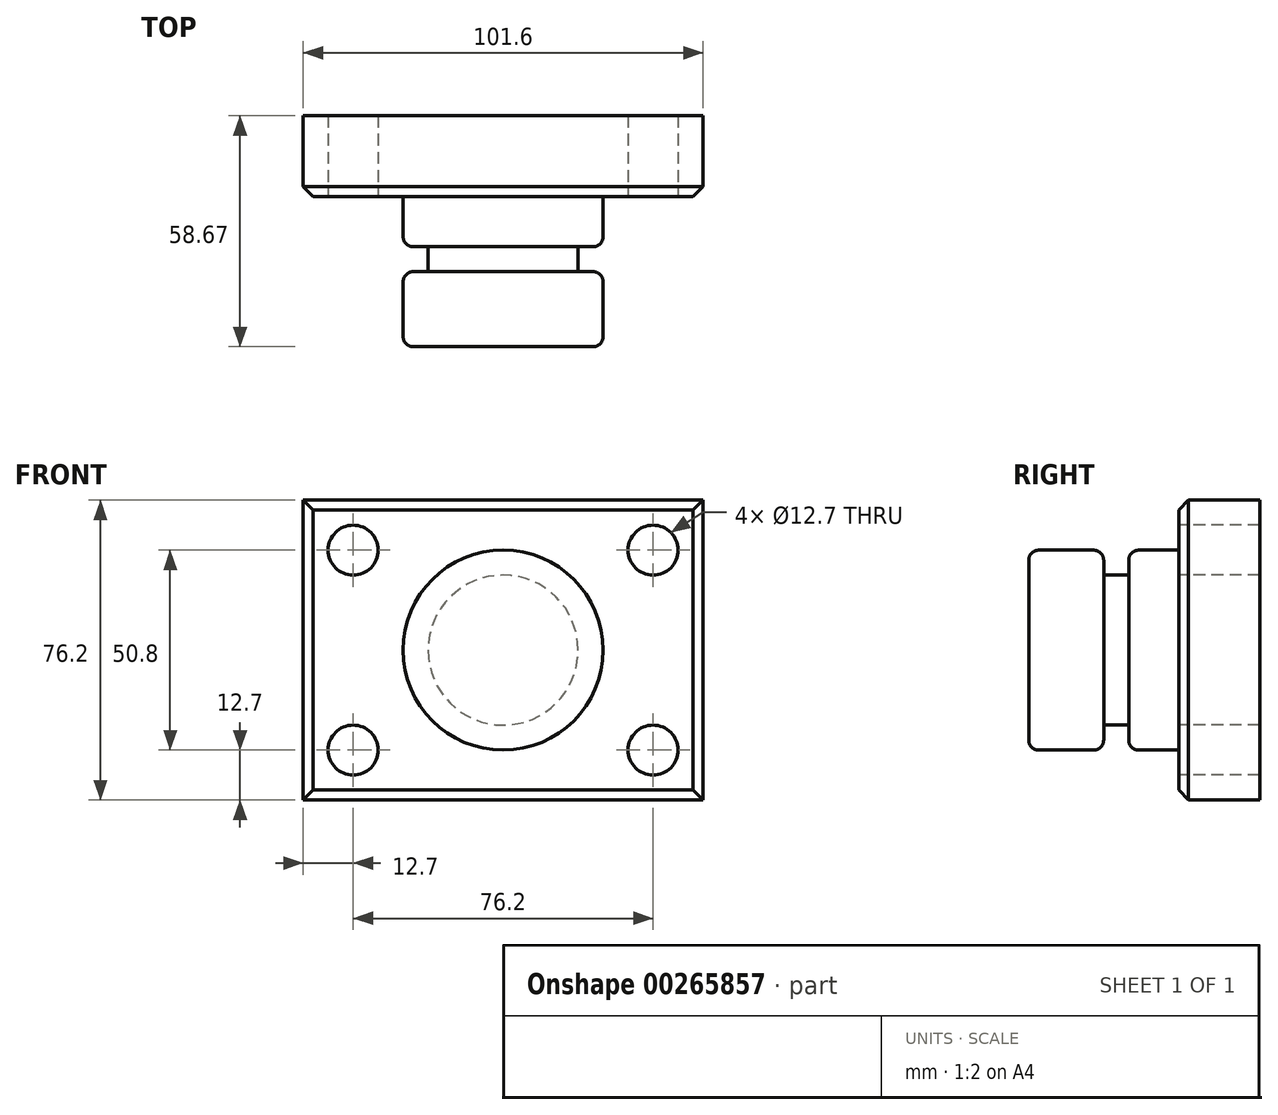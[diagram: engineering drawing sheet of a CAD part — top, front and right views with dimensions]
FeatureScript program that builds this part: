
annotation { "Feature Type Name" : "Feature", "Feature Type Description" : "" }
export const myFeature = defineFeature(function(context is Context, id is Id, definition is map)
    precondition{}
    {
        {
            var Q0;
            Q0=qCreatedBy(makeId("Front.planeOp"),FACE);
            var sketch = newSketch(context, id + "F0", { "sketchPlane" : qUnion([Q0])});
            skLineSegment(sketch, "E0.bottom", {"start": v(50.8, -38.1) * mm, "end": v(-50.8, -38.1) * mm});
            skLineSegment(sketch, "E0.top", {"start": v(50.8, 38.1) * mm, "end": v(-50.8, 38.1) * mm});
            skLineSegment(sketch, "E0.left", {"start": v(50.8, -38.1) * mm, "end": v(50.8, 38.1) * mm});
            skLineSegment(sketch, "E0.right", {"start": v(-50.8, -38.1) * mm, "end": v(-50.8, 38.1) * mm});
            skPoint(sketch, "E0.middle", {"position": v(0, 0) * mm});
            skSolve(sketch);
        }
        {
            var Q0;
            Q0=makeQuery(id+"F0.imprint","IMPRINT",FACE,{"disambiguationData":[TD([[makeQuery(id+"F0.imprint","IMPRINT",EDGE,{"derivedFrom":sQuery(id+"F0.wireOp",EDGE,"E0.bottom")}),-1.0]])]});
            extrude(context, id + "F1", {"entities" : qUnion([Q0]), "depth" : 20.57 * mm});
        }
        {
            var Q0;
            Q0=makeQuery(id+"F1.opExtrude","CAP_FACE",FACE,{"disambiguationData":[OSD([sQuery(id+"F0.wireOp",EDGE,"E0.bottom"),sQuery(id+"F0.wireOp",EDGE,"E0.top"),sQuery(id+"F0.wireOp",EDGE,"E0.left"),sQuery(id+"F0.wireOp",EDGE,"E0.right")])],"isStart":false});
            var sketch = newSketch(context, id + "F2", { "sketchPlane" : qUnion([Q0])});
            skCircle(sketch, "E1", {"center": v(38.1, 25.4) * mm, "radius": 6.35 * mm});
            skCircle(sketch, "E2", {"center": v(38.1, -25.4) * mm, "radius": 6.35 * mm});
            skCircle(sketch, "E3", {"center": v(-38.1, 25.4) * mm, "radius": 6.35 * mm});
            skCircle(sketch, "E4", {"center": v(-38.1, -25.4) * mm, "radius": 6.35 * mm});
            skSolve(sketch);
        }
        {
            var Q0;
            Q0=makeQuery(id+"F2.imprint","IMPRINT",FACE,{"disambiguationData":[TD([[makeQuery(id+"F2.imprint","IMPRINT",EDGE,{"derivedFrom":sQuery(id+"F2.wireOp",EDGE,"E2")}),1.0]])]});
            var Q1;
            Q1=makeQuery(id+"F2.imprint","IMPRINT",FACE,{"disambiguationData":[TD([[makeQuery(id+"F2.imprint","IMPRINT",EDGE,{"derivedFrom":sQuery(id+"F2.wireOp",EDGE,"E4")}),1.0]])]});
            var Q2;
            Q2=makeQuery(id+"F2.imprint","IMPRINT",FACE,{"disambiguationData":[TD([[makeQuery(id+"F2.imprint","IMPRINT",EDGE,{"derivedFrom":sQuery(id+"F2.wireOp",EDGE,"E3")}),1.0]])]});
            var Q3;
            Q3=makeQuery(id+"F2.imprint","IMPRINT",FACE,{"disambiguationData":[TD([[makeQuery(id+"F2.imprint","IMPRINT",EDGE,{"derivedFrom":sQuery(id+"F2.wireOp",EDGE,"E1")}),1.0]])]});
            extrude(context, id + "F3", {"entities" : qUnion([Q0, Q1, Q2, Q3]), "operationType" : NewBodyOperationType.REMOVE, "oppositeDirection" : true, "depth" : 25.4 * mm});
        }
        {
            var Q0;
            Q0=qCreatedBy(makeId("Top.planeOp"),FACE);
            var sketch = newSketch(context, id + "F4", { "sketchPlane" : qUnion([Q0])});
            skLineSegment(sketch, "E5.bottom", {"start": v(0, -58.67) * mm, "end": v(25.4, -58.67) * mm});
            skLineSegment(sketch, "E5.top", {"start": v(0, -20.57) * mm, "end": v(25.4, -20.57) * mm});
            skLineSegment(sketch, "E5.left", {"start": v(0, -58.67) * mm, "end": v(0, -20.57) * mm});
            skLineSegment(sketch, "E5.right", {"start": v(25.4, -58.67) * mm, "end": v(25.4, -20.57) * mm});
            skSolve(sketch);
        }
        {
            var Q0;
            Q0 = qSketchRegion(id + "F4", true);
            var Q1;
            Q1=sQuery(id+"F4.wireOp",EDGE,"E5.left");
            revolve(context, id + "F5", {"operationType" : NewBodyOperationType.ADD, "entities" : qUnion([Q0]), "axis" : qUnion([Q1]), "revolveType" : RevolveType.FULL});
        }
        {
            var Q0;
            Q0=qCreatedBy(makeId("Right.planeOp"),FACE);
            var sketch = newSketch(context, id + "F6", { "sketchPlane" : qUnion([Q0])});
            skLineSegment(sketch, "E6.bottom", {"start": v(-33.27, 19.05) * mm, "end": v(-39.62, 19.05) * mm});
            skLineSegment(sketch, "E6.top", {"start": v(-33.27, 33.32) * mm, "end": v(-39.62, 33.32) * mm});
            skLineSegment(sketch, "E6.left", {"start": v(-33.27, 19.05) * mm, "end": v(-33.27, 33.32) * mm});
            skLineSegment(sketch, "E6.right", {"start": v(-39.62, 19.05) * mm, "end": v(-39.62, 33.32) * mm});
            skPoint(sketch, "E6.middle", {"position": v(-36.45, 26.19) * mm});
            skSolve(sketch);
        }
        {
            var Q0;
            Q0=makeQuery(id+"F6.imprint","IMPRINT",FACE,{"disambiguationData":[TD([[makeQuery(id+"F6.imprint","IMPRINT",EDGE,{"derivedFrom":sQuery(id+"F6.wireOp",EDGE,"E6.bottom")}),-1.0]])]});
            var Q1;
            Q1=makeQuery(id+"F5.opRevolve","SWEPT_FACE",FACE,{"disambiguationData":[OSD([sQuery(id+"F4.wireOp",EDGE,"E5.right")])]});
            revolve(context, id + "F7", {"operationType" : NewBodyOperationType.REMOVE, "entities" : qUnion([Q0]), "axis" : qUnion([Q1]), "revolveType" : RevolveType.FULL, "oppositeDirection" : true});
        }
        {
            var Q0;
            Q0=makeQuery(id+"F1.opExtrude","CAP_EDGE",EDGE,{"disambiguationData":[OSD([sQuery(id+"F0.wireOp",EDGE,"E0.top")])],"isStart":false});
            var Q1;
            Q1=makeQuery(id+"F1.opExtrude","CAP_EDGE",EDGE,{"disambiguationData":[OSD([sQuery(id+"F0.wireOp",EDGE,"E0.left")])],"isStart":false});
            var Q2;
            Q2=makeQuery(id+"F1.opExtrude","CAP_EDGE",EDGE,{"disambiguationData":[OSD([sQuery(id+"F0.wireOp",EDGE,"E0.bottom")])],"isStart":false});
            var Q3;
            Q3=makeQuery(id+"F1.opExtrude","CAP_EDGE",EDGE,{"disambiguationData":[OSD([sQuery(id+"F0.wireOp",EDGE,"E0.right")])],"isStart":false});
            chamfer(context, id + "F8", {"entities" : qUnion([Q0, Q1, Q2, Q3]), "width" : 2.54 * mm, "tangentPropagation" : true});
        }
        {
            var Q0;
            Q0=makeQuery(id+"F5.opRevolve","SWEPT_EDGE",EDGE,{"disambiguationData":[OSD([sQuery(id+"F4.wireOp",EDGE,"E5.top"),sQuery(id+"F4.wireOp",EDGE,"E5.right")])]});
            var Q1;
            Q1=makeQuery(id+"F7.boolean.opBoolean","INTERSECT",EDGE,{"derivedFrom":[makeQuery(id+"F5.opRevolve","SWEPT_FACE",FACE,{"disambiguationData":[OSD([sQuery(id+"F4.wireOp",EDGE,"E5.right")])]}),makeQuery(id+"F7.opRevolve","SWEPT_FACE",FACE,{"disambiguationData":[OSD([sQuery(id+"F6.wireOp",EDGE,"E6.left")])]})]});
            var Q2;
            Q2=makeQuery(id+"F7.boolean.opBoolean","INTERSECT",EDGE,{"derivedFrom":[makeQuery(id+"F5.opRevolve","SWEPT_FACE",FACE,{"disambiguationData":[OSD([sQuery(id+"F4.wireOp",EDGE,"E5.right")])]}),makeQuery(id+"F7.opRevolve","SWEPT_FACE",FACE,{"disambiguationData":[OSD([sQuery(id+"F6.wireOp",EDGE,"E6.right")])]})]});
            fillet(context, id + "F9", {"entities" : qUnion([Q0, Q1, Q2]), "radius" : 2.54 * mm, "tangentPropagation" : true, "allowEdgeOverflow" : false});
        }
        {
            var Q0;
            Q0=makeQuery(id+"F5.opRevolve","SWEPT_EDGE",EDGE,{"disambiguationData":[OSD([sQuery(id+"F4.wireOp",EDGE,"E5.bottom"),sQuery(id+"F4.wireOp",EDGE,"E5.right")])]});
            fillet(context, id + "F10", {"entities" : qUnion([Q0]), "radius" : 2.54 * mm, "tangentPropagation" : true, "allowEdgeOverflow" : false});
        }
    });
